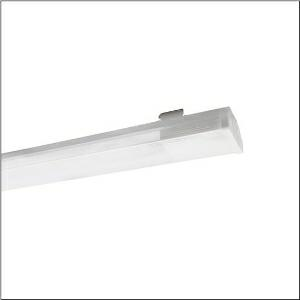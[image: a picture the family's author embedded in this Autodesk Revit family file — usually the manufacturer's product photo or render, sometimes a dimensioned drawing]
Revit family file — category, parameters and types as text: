
# Revit family: modario_r__31_gen_2_53bm812du4gxc2_def8
name_source: partatom
category: Lighting Fixtures
units: mm (PartAtom-declared; Revit-internal decimal feet)

## family parameters
Cut with Voids When Loaded = No
Host = Face
Light Source = No
Part Type = Normal
Room Calculation Point = No
Round Connector Dimension = Use Diameter
Shared = No

## types (1)
- --- (1 x LED, 16290 lm, 92.1 W, 4000K)
    Apparent Load = 92 VA
    CIE Flux Codes = 47 80 95 93 100
    Color Rendering = 80
    Color Temperature = 4000K
    Default Elevation = 1800 mm
    Description = Modario® 31 Gen.2, luminaire insert, of sheet steel, coil coated, white, length: 2.392mm, width: 81mm, height: 82mm, 8x system unit, system units: 299mm, LED rated luminous flux: 16.290lm, light colour: 840, control gear: DALI 2, control gear: ECG DALI, with plug, 5-pole, with phase selection, mains connection: 220..240V, AC, 50/60Hz, rated input power: 92W, through-wiring accessed according to module size, primary optical cover: cover, of PMMA, light emission: direct distribution, primary light characteristic: symmetric, protection rating (complete): IP20, protection rating (LED compartment): IP50, insulation class (complete): insulation class I (protective earthing), certification: CE, ENEC, VDE, UKCA, impact resistance: IK03, permissible ambient temperature for indoor applications: -25..+40°C, corresponds to IFS (International Featured Standards) requirements for safety and quality in the food industry, reducing of maximum allowable ambient temperature of 5°C with ceiling mounting, packaging unit: 1 piece
    Height = 92 mm
    Lamp = 1 x LED
    Lamp Light Flux = 16290 lm
    Lamp Power = 92.1 W
    Lamp count = 1
    Length = 2392 mm
    Luminous efficacy = 177 lm/W
    Manufacturer = Siteco
    ModVariant = No
    Model = 53BM812DU4GXC2
    Mounting Place = Ceiling
    Mounting Type = Pendant
    Number of Poles = 1
    OnlyDefault = Yes
    Power Factor = 1
    Product Name = Modario® 31 Gen.2
    Product group = luminaire insert
    ProductGroupID = 902
    Protection Class = Protection class I
    Protection Degree = IP 20
    RLX_Detail_Level = 1
    RLX_Emergency_Light_Flux = 0 lm
    RLX_Emergency_Type = 0
    RLX_Emergency_Type_DB = No
    RlxData = <blob elided: 38181 chars, md5=45a9d537>
    Socket = socket
    Standby Power = 0 W
    System Light Flux = 16290 lm
    System Power = 92 W
    Type Comments = factory setting: luminous flux: 100 % | dim-lin: 254 | 418 mA
    Type Image = l_1341883.jpg
    URL = http://relux.com
    VarID = @adj_043550
    Voltage = 0 V
    Weight = 0.00 kg
    Width = 81 mm

## geometry (parser evidence)
native form markers: Blend x4, Sweep x12
no freeform markers — native parametric forms only
